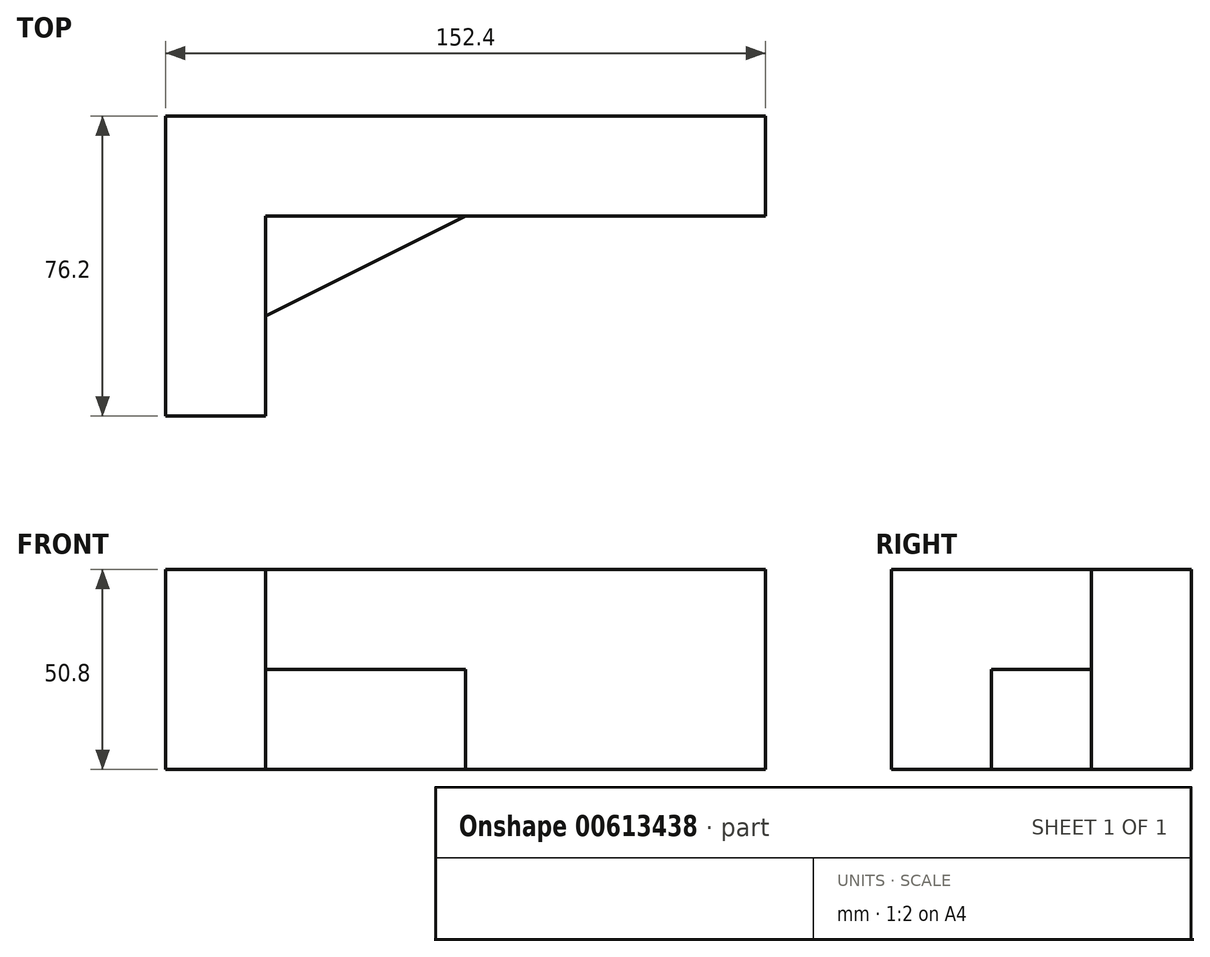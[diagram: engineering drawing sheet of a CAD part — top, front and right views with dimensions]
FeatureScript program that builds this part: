
annotation { "Feature Type Name" : "Feature", "Feature Type Description" : "" }
export const myFeature = defineFeature(function(context is Context, id is Id, definition is map)
    precondition{}
    {
        {
            var Q0;
            Q0=qCreatedBy(makeId("Top.planeOp"),FACE);
            var sketch = newSketch(context, id + "F0", { "sketchPlane" : qUnion([Q0])});
            skLineSegment(sketch, "E0", {"start": v(0, 0) * mm, "end": v(0, 76.2) * mm});
            skLineSegment(sketch, "E1", {"start": v(0, 76.2) * mm, "end": v(152.4, 76.2) * mm});
            skLineSegment(sketch, "E2", {"start": v(152.4, 76.2) * mm, "end": v(152.4, 50.8) * mm});
            skLineSegment(sketch, "E3", {"start": v(152.4, 50.8) * mm, "end": v(76.2, 50.8) * mm});
            skLineSegment(sketch, "E4", {"start": v(76.2, 50.8) * mm, "end": v(25.4, 25.4) * mm});
            skLineSegment(sketch, "E5", {"start": v(25.4, 25.4) * mm, "end": v(25.4, 0) * mm});
            skLineSegment(sketch, "E6", {"start": v(25.4, 0) * mm, "end": v(0, 0) * mm});
            skSolve(sketch);
        }
        {
            var Q0;
            Q0=makeQuery(id+"F0.imprint","IMPRINT",FACE,{"disambiguationData":[TD([[makeQuery(id+"F0.imprint","IMPRINT",EDGE,{"derivedFrom":sQuery(id+"F0.wireOp",EDGE,"E0")}),-1.0]])]});
            extrude(context, id + "F1", {"entities" : qUnion([Q0]), "depth" : 50.8 * mm, "offsetDistance" : 25.4 * mm});
        }
        {
            var Q0;
            Q0=makeQuery(id+"F1.opExtrude","CAP_FACE",FACE,{"disambiguationData":[OSD([sQuery(id+"F0.wireOp",EDGE,"E0"),sQuery(id+"F0.wireOp",EDGE,"E1"),sQuery(id+"F0.wireOp",EDGE,"E2"),sQuery(id+"F0.wireOp",EDGE,"E3"),sQuery(id+"F0.wireOp",EDGE,"E4"),sQuery(id+"F0.wireOp",EDGE,"E5"),sQuery(id+"F0.wireOp",EDGE,"E6")])],"isStart":false});
            var sketch = newSketch(context, id + "F2", { "sketchPlane" : qUnion([Q0])});
            skLineSegment(sketch, "E7", {"start": v(25.4, 25.4) * mm, "end": v(25.4, 50.8) * mm});
            skLineSegment(sketch, "E8", {"start": v(25.4, 50.8) * mm, "end": v(76.2, 50.8) * mm});
            skLineSegment(sketch, "E9", {"start": v(76.2, 50.8) * mm, "end": v(25.4, 25.4) * mm});
            skSolve(sketch);
        }
        {
            var Q0;
            Q0=makeQuery(id+"F2.imprint","IMPRINT",FACE,{"disambiguationData":[TD([[makeQuery(id+"F2.imprint","IMPRINT",EDGE,{"derivedFrom":sQuery(id+"F2.wireOp",EDGE,"E7")}),-1.0]])]});
            extrude(context, id + "F3", {"entities" : qUnion([Q0]), "operationType" : NewBodyOperationType.REMOVE, "oppositeDirection" : true, "depth" : 25.4 * mm, "offsetDistance" : 25.4 * mm});
        }
    });
